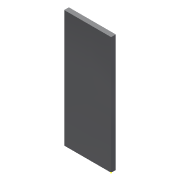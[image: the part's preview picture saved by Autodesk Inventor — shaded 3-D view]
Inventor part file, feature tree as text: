
AUTODESK INVENTOR PART (.ipt)
format: ipt  version: 2018 (Build 220112000, 112)  size: 77,312 bytes
history: native  units: in
note: dims shown in document units (in); Inventor stores cm internally (conversion verified against a paired STEP export)
features: sketch x1
ambient origin geometry x8: Origin, YZ Plane, XZ Plane, XY Plane, X Axis, Y Axis, Z Axis, Center Point
bodies: Solid1 (feature_tree), Body1 (feature_tree)
feature tree (1):
  sketch  "Sketch1"
